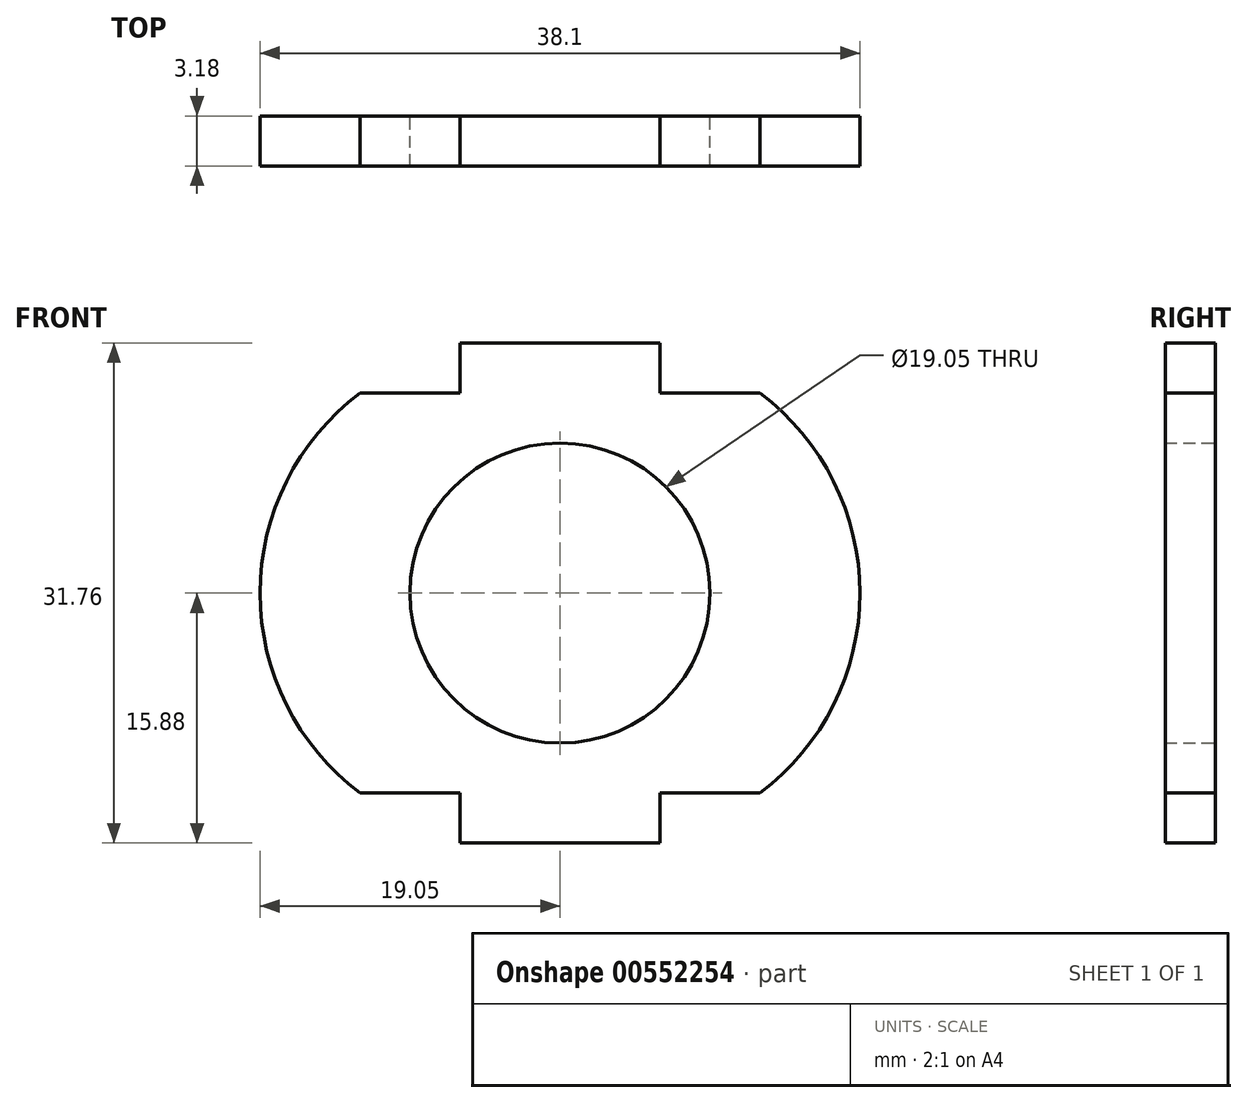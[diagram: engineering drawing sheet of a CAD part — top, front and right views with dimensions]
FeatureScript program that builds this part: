
annotation { "Feature Type Name" : "Feature", "Feature Type Description" : "" }
export const myFeature = defineFeature(function(context is Context, id is Id, definition is map)
    precondition{}
    {
        {
            var Q0;
            Q0=qCreatedBy(makeId("Front.planeOp"),FACE);
            var sketch = newSketch(context, id + "F0", { "sketchPlane" : qUnion([Q0])});
            skCircle(sketch, "E0", {"center": v(0, 0) * mm, "radius": 9.53 * mm});
            skArc(sketch, "E1", {"start": v(-12.7, 12.7) * mm, "mid": v(-19.05, 0) * mm, "end": v(-12.7, -12.7) * mm});
            skArc(sketch, "E2", {"start": v(12.7, -12.7) * mm, "mid": v(19.05, 0) * mm, "end": v(12.7, 12.7) * mm});
            skLineSegment(sketch, "E3", {"start": v(6.35, 12.7) * mm, "end": v(6.35, 15.88) * mm});
            skLineSegment(sketch, "E4.bottom", {"start": v(6.35, 15.88) * mm, "end": v(-6.35, 15.88) * mm});
            skLineSegment(sketch, "E4.left", {"start": v(6.35, 15.88) * mm, "end": v(6.35, 12.7) * mm});
            skLineSegment(sketch, "E4.right", {"start": v(-6.35, 15.88) * mm, "end": v(-6.35, 12.7) * mm});
            skLineSegment(sketch, "E5", {"start": v(6.35, -12.7) * mm, "end": v(6.35, -15.88) * mm});
            skLineSegment(sketch, "E6", {"start": v(6.35, -15.88) * mm, "end": v(-6.35, -15.88) * mm});
            skLineSegment(sketch, "E7.bottom", {"start": v(-6.35, -15.88) * mm, "end": v(6.35, -15.88) * mm});
            skLineSegment(sketch, "E7.left", {"start": v(-6.35, -15.88) * mm, "end": v(-6.35, -12.7) * mm});
            skLineSegment(sketch, "E7.right", {"start": v(6.35, -15.88) * mm, "end": v(6.35, -12.7) * mm});
            skLineSegment(sketch, "E8", {"start": v(-12.7, 12.7) * mm, "end": v(-6.35, 12.7) * mm});
            skLineSegment(sketch, "E9", {"start": v(6.35, 12.7) * mm, "end": v(12.7, 12.7) * mm});
            skLineSegment(sketch, "E10", {"start": v(12.7, -12.7) * mm, "end": v(6.35, -12.7) * mm});
            skLineSegment(sketch, "E11", {"start": v(-6.35, -12.7) * mm, "end": v(-12.7, -12.7) * mm});
            skSolve(sketch);
        }
        {
            var Q0;
            Q0 = qSketchRegion(id + "F0", true);
            extrude(context, id + "F1", {"entities" : qUnion([Q0]), "depth" : 3.17 * mm, "offsetDistance" : 25.4 * mm});
        }
    });
